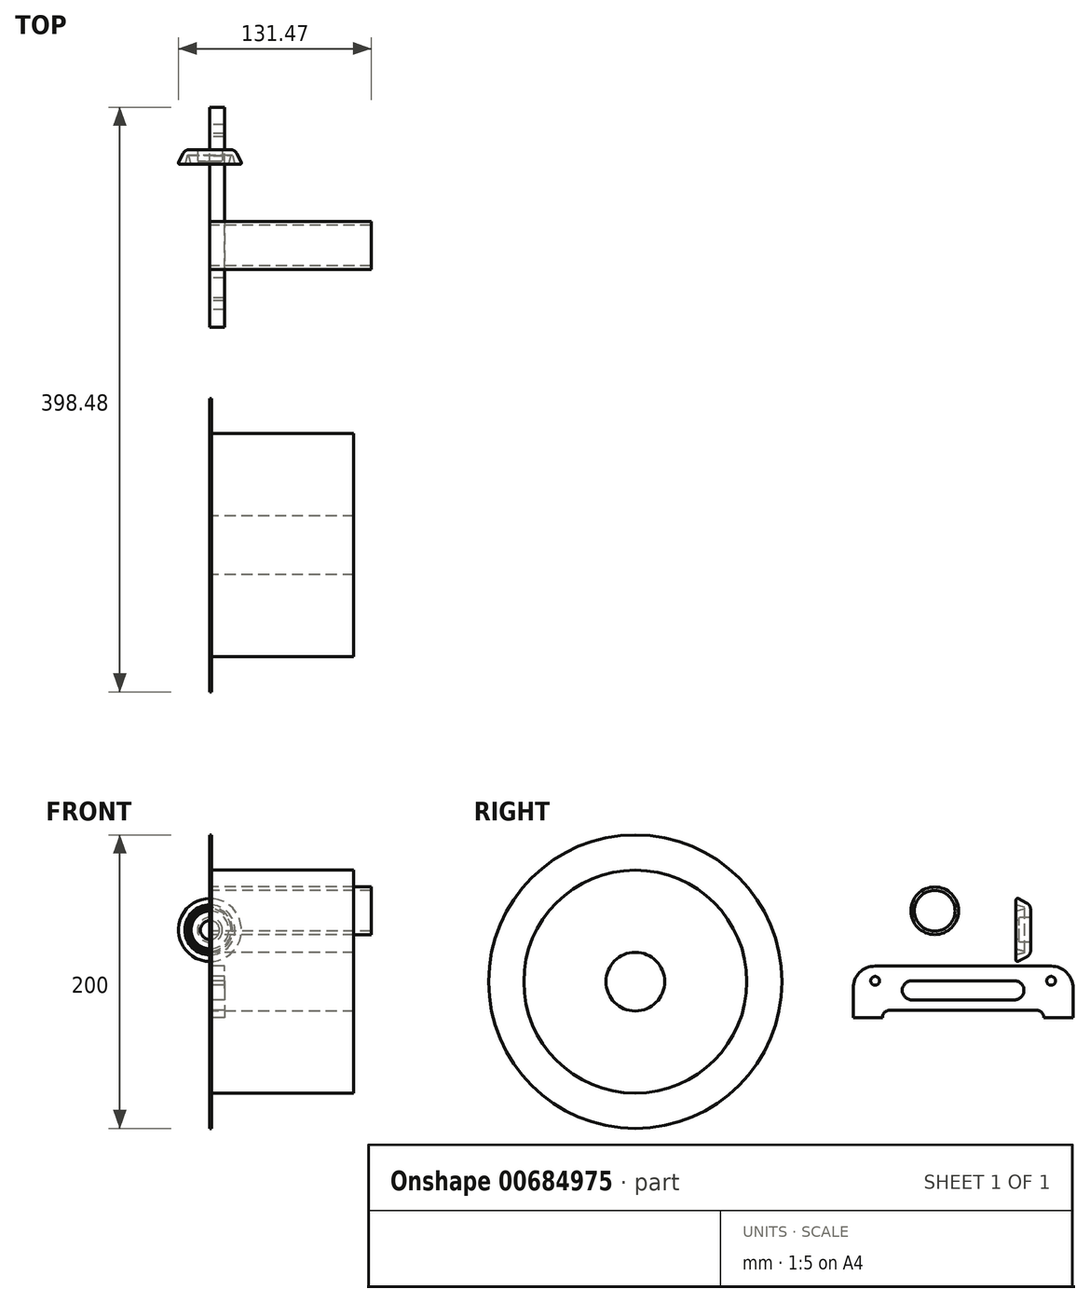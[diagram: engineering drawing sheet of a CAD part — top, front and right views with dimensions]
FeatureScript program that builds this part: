
annotation { "Feature Type Name" : "Feature", "Feature Type Description" : "" }
export const myFeature = defineFeature(function(context is Context, id is Id, definition is map)
    precondition{}
    {
        {
            var Q0;
            Q0=qCreatedBy(makeId("Right.planeOp"),FACE);
            var sketch = newSketch(context, id + "F0", { "sketchPlane" : qUnion([Q0])});
            skCircle(sketch, "E0", {"center": v(-36.35, 24.85) * mm, "radius": 16.25 * mm});
            skCircle(sketch, "E1", {"center": v(-36.35, 24.85) * mm, "radius": 13.9 * mm});
            skLineSegment(sketch, "E2.bottom", {"start": v(-77.02, -12.89) * mm, "end": v(42.98, -12.89) * mm});
            skLineSegment(sketch, "E2.left", {"start": v(-92.02, -27.89) * mm, "end": v(-92.02, -47.89) * mm});
            skLineSegment(sketch, "E2.right", {"start": v(57.98, -27.89) * mm, "end": v(57.98, -47.89) * mm});
            skCircle(sketch, "E3", {"center": v(-77.02, -22.89) * mm, "radius": 3 * mm});
            skCircle(sketch, "E4", {"center": v(42.98, -22.89) * mm, "radius": 3 * mm});
            skCircle(sketch, "E5", {"center": v(-36.35, 24.85) * mm, "radius": 20 * mm});
            skLineSegment(sketch, "E6", {"start": v(19, 32.25) * mm, "end": v(19, 28.88) * mm});
            skLineSegment(sketch, "E7", {"start": v(25, 27.28) * mm, "end": v(25, 26.28) * mm});
            skLineSegment(sketch, "E8", {"start": v(4.26, 11.78) * mm, "end": v(61.35, 11.78) * mm, "construction": true});
            skLineSegment(sketch, "E9", {"start": v(19, 28.88) * mm, "end": v(25, 27.28) * mm});
            skLineSegment(sketch, "E10", {"start": v(20.46, 33.14) * mm, "end": v(26.28, 30.17) * mm});
            skLineSegment(sketch, "E11", {"start": v(29, 25.72) * mm, "end": v(29, 20.28) * mm});
            skLineSegment(sketch, "E12", {"start": v(29, 20.28) * mm, "end": v(21, 20.28) * mm});
            skLineSegment(sketch, "E13", {"start": v(25, 26.28) * mm, "end": v(19, 24.67) * mm});
            skLineSegment(sketch, "E14", {"start": v(19, 18.28) * mm, "end": v(21, 18.28) * mm});
            skLineSegment(sketch, "E15", {"start": v(19, 24.67) * mm, "end": v(19, 18.28) * mm});
            skLineSegment(sketch, "E16", {"start": v(21, 20.28) * mm, "end": v(21, 18.28) * mm});
            skPoint(sketch, "E17.visualSharp", {"position": v(29, 28.78) * mm});
            skArc(sketch, "E17.filletArc", {"start": v(29, 25.72) * mm, "mid": v(28.27, 28.33) * mm, "end": v(26.28, 30.17) * mm});
            skPoint(sketch, "E18.visualSharp", {"position": v(19, 33.88) * mm});
            skArc(sketch, "E18.filletArc", {"start": v(20.46, 33.14) * mm, "mid": v(19.49, 33.1) * mm, "end": v(19, 32.25) * mm});
            skCircle(sketch, "E19", {"center": v(-240.5, -23.46) * mm, "radius": 100 * mm});
            skCircle(sketch, "E20", {"center": v(-240.5, -23.46) * mm, "radius": 20 * mm});
            skCircle(sketch, "E21", {"center": v(-240.5, -23.46) * mm, "radius": 76 * mm});
            skPoint(sketch, "E22.visualSharp", {"position": v(57.98, -12.89) * mm});
            skArc(sketch, "E22.filletArc", {"start": v(57.98, -27.89) * mm, "mid": v(53.58, -17.28) * mm, "end": v(42.98, -12.89) * mm});
            skPoint(sketch, "E23.visualSharp", {"position": v(-92.02, -12.89) * mm});
            skArc(sketch, "E23.filletArc", {"start": v(-77.02, -12.89) * mm, "mid": v(-87.63, -17.28) * mm, "end": v(-92.02, -27.89) * mm});
            skLineSegment(sketch, "E24", {"start": v(32.98, -42.89) * mm, "end": v(-67.02, -42.89) * mm});
            skLineSegment(sketch, "E25", {"start": v(37.98, -47.89) * mm, "end": v(37.98, -47.89) * mm});
            skLineSegment(sketch, "E26", {"start": v(37.98, -47.89) * mm, "end": v(57.98, -47.89) * mm});
            skLineSegment(sketch, "E27", {"start": v(-72.02, -47.89) * mm, "end": v(-72.02, -47.89) * mm});
            skLineSegment(sketch, "E28", {"start": v(-72.02, -47.89) * mm, "end": v(-92.02, -47.89) * mm});
            skPoint(sketch, "E29.visualSharp", {"position": v(37.98, -42.89) * mm});
            skArc(sketch, "E29.filletArc", {"start": v(37.98, -47.89) * mm, "mid": v(36.51, -44.35) * mm, "end": v(32.98, -42.89) * mm});
            skPoint(sketch, "E30.visualSharp", {"position": v(-72.02, -42.89) * mm});
            skArc(sketch, "E30.filletArc", {"start": v(-67.02, -42.89) * mm, "mid": v(-70.56, -44.35) * mm, "end": v(-72.02, -47.89) * mm});
            skLineSegment(sketch, "E31", {"start": v(17.98, -22.89) * mm, "end": v(-52.02, -22.89) * mm});
            skLineSegment(sketch, "E32", {"start": v(17.98, -35.89) * mm, "end": v(-52.02, -35.89) * mm});
            skArc(sketch, "E33", {"start": v(-52.02, -22.89) * mm, "mid": v(-58.52, -29.39) * mm, "end": v(-52.02, -35.89) * mm});
            skArc(sketch, "E34", {"start": v(17.98, -22.89) * mm, "mid": v(24.48, -29.39) * mm, "end": v(17.98, -35.89) * mm});
            skSolve(sketch);
        }
        {
            var Q0;
            Q0=makeQuery(id+"F0.imprint","IMPRINT",FACE,{"disambiguationData":[TD([[makeQuery(id+"F0.imprint","IMPRINT",EDGE,{"derivedFrom":sQuery(id+"F0.wireOp",EDGE,"E6")}),1.0]])]});
            var Q1;
            Q1=sQuery(id+"F0.wireOp",EDGE,"E8");
            revolve(context, id + "F1", {"entities" : qUnion([Q0]), "axis" : qUnion([Q1]), "revolveType" : RevolveType.FULL});
        }
        {
            var Q0;
            Q0=makeQuery(id+"F0.imprint","IMPRINT",FACE,{"disambiguationData":[TD([[makeQuery(id+"F0.imprint","IMPRINT",EDGE,{"derivedFrom":sQuery(id+"F0.wireOp",EDGE,"E0")}),1.0]])]});
            extrude(context, id + "F2", {"entities" : qUnion([Q0]), "depth" : 110 * mm, "offsetDistance" : 25 * mm});
        }
        {
            var Q0;
            Q0=makeQuery(id+"F0.imprint","IMPRINT",FACE,{"disambiguationData":[TD([[makeQuery(id+"F0.imprint","IMPRINT",EDGE,{"derivedFrom":sQuery(id+"F0.wireOp",EDGE,"E19")}),1.0]])]});
            var Q1;
            Q1=makeQuery(id+"F0.imprint","IMPRINT",FACE,{"disambiguationData":[TD([[makeQuery(id+"F0.imprint","IMPRINT",EDGE,{"derivedFrom":sQuery(id+"F0.wireOp",EDGE,"E20")}),-1.0]])]});
            extrude(context, id + "F3", {"entities" : qUnion([Q0, Q1]), "depth" : 1 * mm, "offsetDistance" : 25 * mm});
        }
        {
            var Q0;
            Q0=makeQuery(id+"F0.imprint","IMPRINT",FACE,{"disambiguationData":[TD([[makeQuery(id+"F0.imprint","IMPRINT",EDGE,{"derivedFrom":sQuery(id+"F0.wireOp",EDGE,"E20")}),-1.0]])]});
            extrude(context, id + "F4", {"entities" : qUnion([Q0]), "depth" : 98 * mm, "offsetDistance" : 25 * mm});
        }
        {
            var Q0;
            Q0=makeQuery(id+"F0.imprint","IMPRINT",FACE,{"disambiguationData":[TD([[makeQuery(id+"F0.imprint","IMPRINT",EDGE,{"derivedFrom":sQuery(id+"F0.wireOp",EDGE,"E2.bottom")}),-1.0]])]});
            extrude(context, id + "F5", {"entities" : qUnion([Q0]), "depth" : 10 * mm, "offsetDistance" : 25 * mm});
        }
    });
